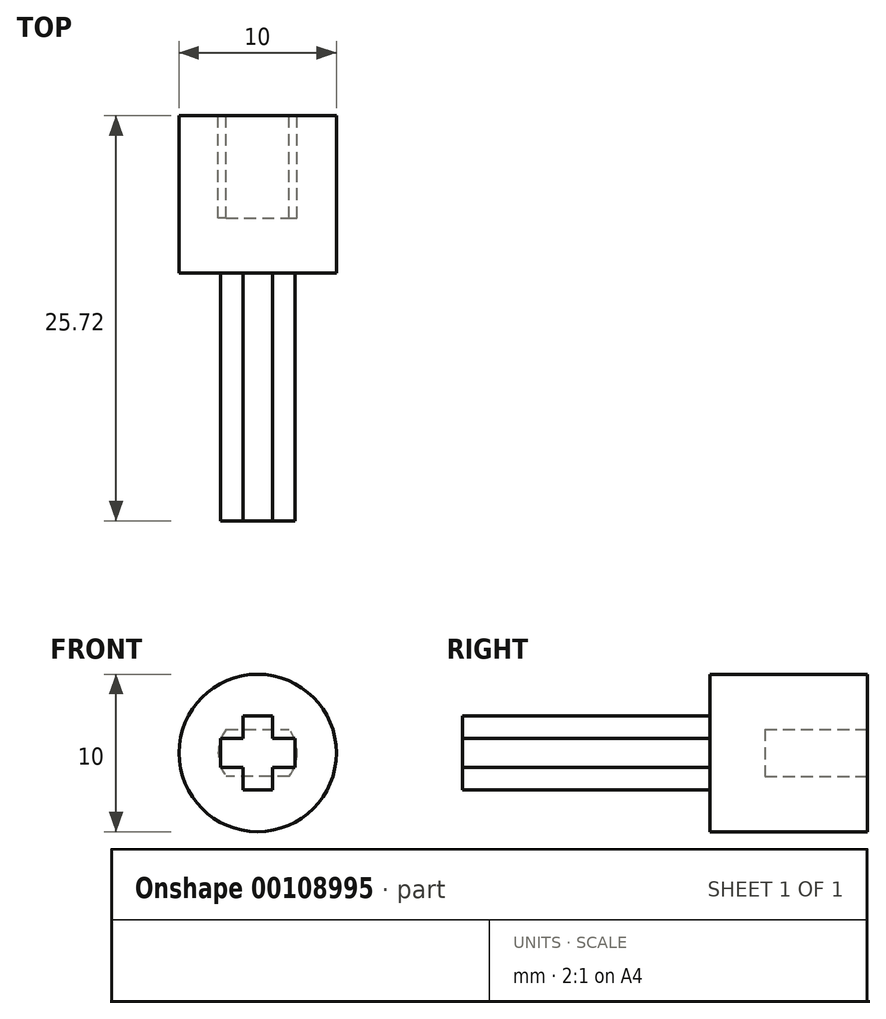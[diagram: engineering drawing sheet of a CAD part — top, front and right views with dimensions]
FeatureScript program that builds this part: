
annotation { "Feature Type Name" : "Feature", "Feature Type Description" : "" }
export const myFeature = defineFeature(function(context is Context, id is Id, definition is map)
    precondition{}
    {
        {
            var Q0;
            Q0=qCreatedBy(makeId("Front.planeOp"),FACE);
            var sketch = newSketch(context, id + "F0", { "sketchPlane" : qUnion([Q0])});
            skLineSegment(sketch, "E0", {"start": v(0.93, 2.36) * mm, "end": v(0.93, 0.93) * mm});
            skLineSegment(sketch, "E1", {"start": v(0.93, 0.93) * mm, "end": v(2.36, 0.93) * mm});
            skLineSegment(sketch, "E2", {"start": v(2.36, 0.93) * mm, "end": v(2.36, -0.93) * mm});
            skLineSegment(sketch, "E3", {"start": v(2.36, -0.93) * mm, "end": v(0.93, -0.93) * mm});
            skLineSegment(sketch, "E4", {"start": v(0.93, -0.93) * mm, "end": v(0.93, -2.36) * mm});
            skLineSegment(sketch, "E5", {"start": v(0.93, -2.36) * mm, "end": v(-0.93, -2.36) * mm});
            skLineSegment(sketch, "E6", {"start": v(-0.93, -2.36) * mm, "end": v(-0.93, -0.93) * mm});
            skLineSegment(sketch, "E7", {"start": v(-0.93, -0.93) * mm, "end": v(-2.36, -0.93) * mm});
            skLineSegment(sketch, "E8", {"start": v(-2.36, -0.93) * mm, "end": v(-2.36, 0.93) * mm});
            skLineSegment(sketch, "E9", {"start": v(-2.36, 0.93) * mm, "end": v(-0.93, 0.93) * mm});
            skLineSegment(sketch, "E10", {"start": v(-0.93, 0.93) * mm, "end": v(-0.93, 2.36) * mm});
            skLineSegment(sketch, "E11", {"start": v(-0.93, 2.36) * mm, "end": v(0.93, 2.36) * mm});
            skSolve(sketch);
        }
        {
            var Q0;
            Q0 = qSketchRegion(id + "F0", true);
            extrude(context, id + "F1", {"entities" : qUnion([Q0]), "depth" : 15.72 * mm});
        }
        {
            var Q0;
            Q0=makeQuery(id+"F1.opExtrude","CAP_FACE",FACE,{"disambiguationData":[OSD([sQuery(id+"F0.wireOp",EDGE,"E0"),sQuery(id+"F0.wireOp",EDGE,"E1"),sQuery(id+"F0.wireOp",EDGE,"E2"),sQuery(id+"F0.wireOp",EDGE,"E3"),sQuery(id+"F0.wireOp",EDGE,"E4"),sQuery(id+"F0.wireOp",EDGE,"E5"),sQuery(id+"F0.wireOp",EDGE,"E6"),sQuery(id+"F0.wireOp",EDGE,"E7"),sQuery(id+"F0.wireOp",EDGE,"E8"),sQuery(id+"F0.wireOp",EDGE,"E9"),sQuery(id+"F0.wireOp",EDGE,"E10"),sQuery(id+"F0.wireOp",EDGE,"E11")])],"isStart":true});
            var sketch = newSketch(context, id + "F2", { "sketchPlane" : qUnion([Q0])});
            skCircle(sketch, "E12", {"center": v(0, 0) * mm, "radius": 5 * mm});
            skSolve(sketch);
        }
        {
            var Q0;
            Q0 = qSketchRegion(id + "F2", true);
            extrude(context, id + "F3", {"entities" : qUnion([Q0]), "operationType" : NewBodyOperationType.ADD, "depth" : 10 * mm});
        }
        {
            var Q0;
            Q0=makeQuery(id+"F3.opExtrude","CAP_FACE",FACE,{"disambiguationData":[OSD([sQuery(id+"F2.wireOp",EDGE,"E12")])],"isStart":false});
            var sketch = newSketch(context, id + "F4", { "sketchPlane" : qUnion([Q0])});
            skLineSegment(sketch, "E13", {"start": v(2, 1.5) * mm, "end": v(-2, 1.5) * mm});
            skLineSegment(sketch, "E14", {"start": v(-2, -1.5) * mm, "end": v(2, -1.5) * mm});
            skArc(sketch, "E15", {"start": v(-2, 1.5) * mm, "mid": v(-2.5, 0) * mm, "end": v(-2, -1.5) * mm});
            skArc(sketch, "E16.trimOffspring", {"start": v(2, -1.5) * mm, "mid": v(2.5, 0) * mm, "end": v(2, 1.5) * mm});
            skSolve(sketch);
        }
        {
            var Q0;
            Q0=makeQuery(id+"F4.imprint","IMPRINT",FACE,{"disambiguationData":[TD([[makeQuery(id+"F4.imprint","IMPRINT",EDGE,{"derivedFrom":sQuery(id+"F4.wireOp",EDGE,"E13")}),1.0]])]});
            extrude(context, id + "F5", {"entities" : qUnion([Q0]), "operationType" : NewBodyOperationType.REMOVE, "oppositeDirection" : true, "depth" : 6.5 * mm});
        }
    });
